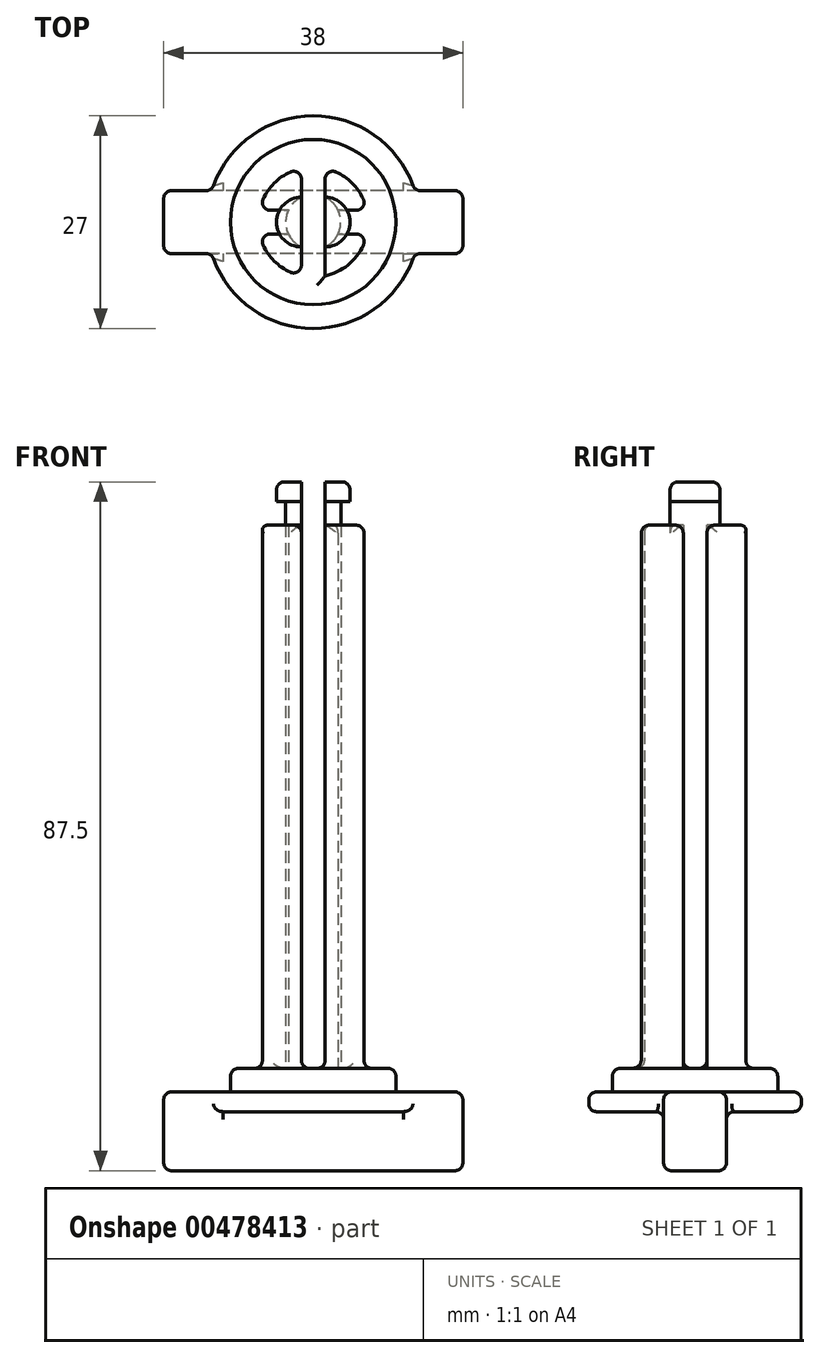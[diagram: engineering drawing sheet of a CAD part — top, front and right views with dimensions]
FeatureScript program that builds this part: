
annotation { "Feature Type Name" : "Feature", "Feature Type Description" : "" }
export const myFeature = defineFeature(function(context is Context, id is Id, definition is map)
    precondition{}
    {
        {
            var Q0;
            Q0=qCreatedBy(makeId("Top.planeOp"),FACE);
            var sketch = newSketch(context, id + "F0", { "sketchPlane" : qUnion([Q0])});
            skLineSegment(sketch, "E0.bottom", {"start": v(19, -4) * mm, "end": v(-19, -4) * mm});
            skLineSegment(sketch, "E0.top", {"start": v(19, 4) * mm, "end": v(-19, 4) * mm});
            skLineSegment(sketch, "E0.left", {"start": v(19, -4) * mm, "end": v(19, 4) * mm});
            skLineSegment(sketch, "E0.right", {"start": v(-19, -4) * mm, "end": v(-19, 4) * mm});
            skPoint(sketch, "E0.middle", {"position": v(0, 0) * mm});
            skSolve(sketch);
        }
        {
            var Q0;
            Q0 = qSketchRegion(id + "F0", true);
            extrude(context, id + "F1", {"entities" : qUnion([Q0]), "depth" : 10 * mm});
        }
        {
            var Q0;
            Q0=makeQuery(id+"F1.opExtrude","CAP_FACE",FACE,{"disambiguationData":[OSD([sQuery(id+"F0.wireOp",EDGE,"E0.bottom"),sQuery(id+"F0.wireOp",EDGE,"E0.top"),sQuery(id+"F0.wireOp",EDGE,"E0.left"),sQuery(id+"F0.wireOp",EDGE,"E0.right")])],"isStart":false});
            var sketch = newSketch(context, id + "F2", { "sketchPlane" : qUnion([Q0])});
            skCircle(sketch, "E1", {"center": v(0, 0) * mm, "radius": 13.5 * mm});
            skSolve(sketch);
        }
        {
            var Q0;
            Q0 = qSketchRegion(id + "F2", true);
            extrude(context, id + "F3", {"entities" : qUnion([Q0]), "operationType" : NewBodyOperationType.ADD, "depth" : -2.5 * mm});
        }
        {
            var Q0;
            Q0=makeQuery(id+"F3.boolean.opBoolean","MERGE",FACE,{"derivedFrom":[makeQuery(id+"F1.opExtrude","CAP_FACE",FACE,{"disambiguationData":[OSD([sQuery(id+"F0.wireOp",EDGE,"E0.bottom"),sQuery(id+"F0.wireOp",EDGE,"E0.top"),sQuery(id+"F0.wireOp",EDGE,"E0.left"),sQuery(id+"F0.wireOp",EDGE,"E0.right")])],"isStart":false}),makeQuery(id+"F3.opExtrude","CAP_FACE",FACE,{"disambiguationData":[OSD([sQuery(id+"F2.wireOp",EDGE,"E1")])],"isStart":true})]});
            var sketch = newSketch(context, id + "F4", { "sketchPlane" : qUnion([Q0])});
            skCircle(sketch, "E2", {"center": v(0, 0) * mm, "radius": 10.5 * mm});
            skSolve(sketch);
        }
        {
            var Q0;
            Q0 = qSketchRegion(id + "F4", true);
            extrude(context, id + "F5", {"entities" : qUnion([Q0]), "operationType" : NewBodyOperationType.ADD, "depth" : 3 * mm});
        }
        {
            var Q0;
            Q0=makeQuery(id+"F3.boolean.opBoolean","MERGE",FACE,{"derivedFrom":[makeQuery(id+"F1.opExtrude","CAP_FACE",FACE,{"disambiguationData":[OSD([sQuery(id+"F0.wireOp",EDGE,"E0.bottom"),sQuery(id+"F0.wireOp",EDGE,"E0.top"),sQuery(id+"F0.wireOp",EDGE,"E0.left"),sQuery(id+"F0.wireOp",EDGE,"E0.right")])],"isStart":false}),makeQuery(id+"F3.opExtrude","CAP_FACE",FACE,{"disambiguationData":[OSD([sQuery(id+"F2.wireOp",EDGE,"E1")])],"isStart":true})]});
            var sketch = newSketch(context, id + "F6", { "sketchPlane" : qUnion([Q0])});
            skArc(sketch, "E3", {"start": v(6.84, 1.5) * mm, "mid": v(0, 7) * mm, "end": v(-6.84, 1.5) * mm, "construction": true});
            skLineSegment(sketch, "E4.bottom", {"start": v(-1.5, -6.84) * mm, "end": v(1.5, -6.84) * mm, "construction": true});
            skLineSegment(sketch, "E4.top", {"start": v(-1.5, 6.84) * mm, "end": v(1.5, 6.84) * mm, "construction": true});
            skLineSegment(sketch, "E4.left", {"start": v(-1.5, -6.84) * mm, "end": v(-1.5, 6.84) * mm, "construction": true});
            skLineSegment(sketch, "E4.right", {"start": v(1.5, -6.84) * mm, "end": v(1.5, 6.84) * mm, "construction": true});
            skArc(sketch, "E5", {"start": v(1.5, -6.84) * mm, "mid": v(4.95, -4.95) * mm, "end": v(6.84, -1.5) * mm});
            skArc(sketch, "E6", {"start": v(-1.5, 6.84) * mm, "mid": v(-4.95, 4.95) * mm, "end": v(-6.84, 1.5) * mm});
            skLineSegment(sketch, "E7", {"start": v(1.5, 6.84) * mm, "end": v(1.5, -6.84) * mm});
            skLineSegment(sketch, "E8", {"start": v(-1.5, -6.84) * mm, "end": v(-1.5, 6.84) * mm});
            skCircle(sketch, "E9", {"center": v(0, 0) * mm, "radius": 3.5 * mm, "construction": true});
            skLineSegment(sketch, "E10.bottom", {"start": v(-6.84, 1.5) * mm, "end": v(6.84, 1.5) * mm, "construction": true});
            skLineSegment(sketch, "E10.top", {"start": v(-6.84, -1.5) * mm, "end": v(6.84, -1.5) * mm, "construction": true});
            skLineSegment(sketch, "E10.left", {"start": v(-6.84, 1.5) * mm, "end": v(-6.84, -1.5) * mm, "construction": true});
            skLineSegment(sketch, "E10.right", {"start": v(6.84, 1.5) * mm, "end": v(6.84, -1.5) * mm, "construction": true});
            skArc(sketch, "E11", {"start": v(-3.16, -1.5) * mm, "mid": v(-3.5, 0) * mm, "end": v(-3.16, 1.5) * mm});
            skArc(sketch, "E12", {"start": v(3.16, -1.5) * mm, "mid": v(3.5, 0) * mm, "end": v(3.16, 1.5) * mm});
            skLineSegment(sketch, "E13", {"start": v(-3.16, -1.5) * mm, "end": v(-6.84, -1.5) * mm});
            skLineSegment(sketch, "E14", {"start": v(-3.16, 1.5) * mm, "end": v(-6.84, 1.5) * mm});
            skLineSegment(sketch, "E15", {"start": v(3.16, 1.5) * mm, "end": v(6.84, 1.5) * mm});
            skLineSegment(sketch, "E16", {"start": v(3.16, -1.5) * mm, "end": v(6.84, -1.5) * mm});
            skArc(sketch, "E17.trimOffspring", {"start": v(-6.84, -1.5) * mm, "mid": v(0, -7) * mm, "end": v(6.84, -1.5) * mm, "construction": true});
            skArc(sketch, "E18.trimOffspring", {"start": v(-6.84, -1.5) * mm, "mid": v(-4.95, -4.95) * mm, "end": v(-1.5, -6.84) * mm});
            skArc(sketch, "E19.trimOffspring", {"start": v(6.84, 1.5) * mm, "mid": v(4.95, 4.95) * mm, "end": v(1.5, 6.84) * mm});
            skSolve(sketch);
        }
        {
            var Q0;
            Q0 = qSketchRegion(id + "F6", true);
            extrude(context, id + "F7", {"entities" : qUnion([Q0]), "operationType" : NewBodyOperationType.ADD, "depth" : 72 * mm});
        }
        {
            var Q0;
            Q0=makeQuery(id+"F7.opExtrude","CAP_FACE",FACE,{"disambiguationData":[OSD([sQuery(id+"F6.wireOp",EDGE,"E5"),sQuery(id+"F6.wireOp",EDGE,"E7")])],"isStart":false});
            var sketch = newSketch(context, id + "F8", { "sketchPlane" : qUnion([Q0])});
            skLineSegment(sketch, "E20.0", {"start": v(1.5, -6.84) * mm, "end": v(1.5, -6.84) * mm});
            skLineSegment(sketch, "E21.0", {"start": v(-1.5, 6.84) * mm, "end": v(-1.5, 6.84) * mm});
            skCircle(sketch, "E22", {"center": v(0, 0) * mm, "radius": 3.5 * mm, "construction": true});
            skArc(sketch, "E23", {"start": v(1.5, -3.16) * mm, "mid": v(3.5, 0) * mm, "end": v(1.5, 3.16) * mm});
            skArc(sketch, "E24", {"start": v(-1.5, 3.16) * mm, "mid": v(-3.5, 0) * mm, "end": v(-1.5, -3.16) * mm});
            skLineSegment(sketch, "E25", {"start": v(1.5, -3.16) * mm, "end": v(1.5, 3.16) * mm});
            skLineSegment(sketch, "E26", {"start": v(-1.5, 3.16) * mm, "end": v(-1.5, -3.16) * mm});
            skSolve(sketch);
        }
        {
            var Q0;
            Q0 = qSketchRegion(id + "F8", true);
            extrude(context, id + "F9", {"entities" : qUnion([Q0]), "operationType" : NewBodyOperationType.ADD, "depth" : 3 * mm});
        }
        {
            var Q0;
            Q0=makeQuery(id+"F9.opExtrude","CAP_FACE",FACE,{"disambiguationData":[OSD([sQuery(id+"F8.wireOp",EDGE,"E24"),sQuery(id+"F8.wireOp",EDGE,"E26")])],"isStart":false});
            var sketch = newSketch(context, id + "F10", { "sketchPlane" : qUnion([Q0])});
            skLineSegment(sketch, "E27.0", {"start": v(1.5, -3.16) * mm, "end": v(1.5, -6.84) * mm, "construction": true});
            skLineSegment(sketch, "E28.0", {"start": v(1.5, 3.16) * mm, "end": v(1.5, -3.16) * mm, "construction": true});
            skLineSegment(sketch, "E29.0", {"start": v(-1.5, 3.16) * mm, "end": v(-1.5, -3.16) * mm, "construction": true});
            skPoint(sketch, "E30.0", {"position": v(0, 0) * mm});
            skArc(sketch, "E31", {"start": v(1.5, 3.16) * mm, "mid": v(4.66, 0) * mm, "end": v(1.5, -3.16) * mm});
            skArc(sketch, "E32", {"start": v(-1.5, -3.16) * mm, "mid": v(-4.66, 0) * mm, "end": v(-1.5, 3.16) * mm});
            skLineSegment(sketch, "E33", {"start": v(-1.5, 3.16) * mm, "end": v(-1.5, -3.16) * mm});
            skLineSegment(sketch, "E34", {"start": v(1.5, -3.16) * mm, "end": v(1.5, 3.16) * mm});
            skSolve(sketch);
        }
        {
            var Q0;
            Q0 = qSketchRegion(id + "F10", true);
            extrude(context, id + "F11", {"entities" : qUnion([Q0]), "operationType" : NewBodyOperationType.ADD, "depth" : 2.5 * mm});
        }
        {
            var Q0;
            Q0=makeQuery(id+"F7.opExtrude","CAP_EDGE",EDGE,{"disambiguationData":[OSD([sQuery(id+"F6.wireOp",EDGE,"E5")])],"isStart":false});
            var Q1;
            Q1=makeQuery(id+"F7.opExtrude","CAP_EDGE",EDGE,{"disambiguationData":[OSD([sQuery(id+"F6.wireOp",EDGE,"E6")])],"isStart":false});
            var Q2;
            Q2=makeQuery(id+"F11.opExtrude","CAP_EDGE",EDGE,{"disambiguationData":[OSD([sQuery(id+"F10.wireOp",EDGE,"OLtfRIEC-O7za-MDvR-deQH-UAJOeCopyKRy")])],"isStart":false});
            var Q3;
            Q3=makeQuery(id+"F11.opExtrude","CAP_EDGE",EDGE,{"disambiguationData":[OSD([sQuery(id+"F10.wireOp",EDGE,"Nmxz0keU-6gQF-4ana-PDwX-EkidwWlCpvxk")])],"isStart":false});
            var Q4;
            Q4=makeQuery(id+"F7.boolean.opBoolean","INTERSECT",EDGE,{"derivedFrom":[makeQuery(id+"F5.opExtrude","CAP_FACE",FACE,{"disambiguationData":[OSD([sQuery(id+"F4.wireOp",EDGE,"E2")])],"isStart":false}),makeQuery(id+"F7.opExtrude","SWEPT_FACE",FACE,{"disambiguationData":[OSD([sQuery(id+"F6.wireOp",EDGE,"E6")])]})]});
            var Q5;
            Q5=makeQuery(id+"F7.boolean.opBoolean","INTERSECT",EDGE,{"derivedFrom":[makeQuery(id+"F5.opExtrude","CAP_FACE",FACE,{"disambiguationData":[OSD([sQuery(id+"F4.wireOp",EDGE,"E2")])],"isStart":false}),makeQuery(id+"F7.opExtrude","SWEPT_FACE",FACE,{"disambiguationData":[OSD([sQuery(id+"F6.wireOp",EDGE,"E5")])]})]});
            var Q6;
            Q6=makeQuery(id+"F7.boolean.opBoolean","INTERSECT",EDGE,{"derivedFrom":[makeQuery(id+"F5.opExtrude","CAP_FACE",FACE,{"disambiguationData":[OSD([sQuery(id+"F4.wireOp",EDGE,"E2")])],"isStart":false}),makeQuery(id+"F7.opExtrude","SWEPT_FACE",FACE,{"disambiguationData":[OSD([sQuery(id+"F6.wireOp",EDGE,"E8")])]})]});
            var Q7;
            Q7=makeQuery(id+"F7.boolean.opBoolean","INTERSECT",EDGE,{"derivedFrom":[makeQuery(id+"F5.opExtrude","CAP_FACE",FACE,{"disambiguationData":[OSD([sQuery(id+"F4.wireOp",EDGE,"E2")])],"isStart":false}),makeQuery(id+"F7.opExtrude","SWEPT_FACE",FACE,{"disambiguationData":[OSD([sQuery(id+"F6.wireOp",EDGE,"E7")])]})]});
            var Q8;
            Q8=makeQuery(id+"F5.opExtrude","CAP_EDGE",EDGE,{"disambiguationData":[OSD([sQuery(id+"F4.wireOp",EDGE,"E2")])],"isStart":false});
            var Q9;
            {var subQ0=sQuery(id+"F0.wireOp",EDGE,"E0.top");var subQ1=sQuery(id+"F2.wireOp",EDGE,"E1");Q9=makeQuery(id+"F3.boolean.opBoolean","SPLIT",EDGE,{"disambiguationData":[TD([makeQuery(id+"F1.opExtrude","SWEPT_FACE",FACE,{"disambiguationData":[OSD([subQ0])]})])],"derivedFrom":makeQuery(id+"F3.opExtrude","CAP_EDGE",EDGE,{"disambiguationData":[OSD([subQ1])],"isStart":true})});}
            var Q10;
            {var subQ0=sQuery(id+"F0.wireOp",EDGE,"E0.right");var subQ2=sQuery(id+"F0.wireOp",EDGE,"E0.top");Q10=makeQuery(id+"F3.boolean.opBoolean","SPLIT",EDGE,{"disambiguationData":[TD([makeQuery(id+"F1.opExtrude","SWEPT_FACE",FACE,{"disambiguationData":[OSD([subQ0])]})])],"derivedFrom":makeQuery(id+"F1.opExtrude","CAP_EDGE",EDGE,{"disambiguationData":[OSD([subQ2])],"isStart":false})});}
            var Q11;
            Q11=makeQuery(id+"F1.opExtrude","CAP_EDGE",EDGE,{"disambiguationData":[OSD([sQuery(id+"F0.wireOp",EDGE,"E0.right")])],"isStart":false});
            var Q12;
            Q12=makeQuery(id+"F1.opExtrude","SWEPT_EDGE",EDGE,{"disambiguationData":[OSD([sQuery(id+"F0.wireOp",EDGE,"E0.top"),sQuery(id+"F0.wireOp",EDGE,"E0.right")])]});
            var Q13;
            Q13=makeQuery(id+"F3.boolean.opBoolean","INTERSECT",EDGE,{"disambiguationData":[OD(1.0)],"derivedFrom":[makeQuery(id+"F1.opExtrude","SWEPT_FACE",FACE,{"disambiguationData":[OSD([sQuery(id+"F0.wireOp",EDGE,"E0.top")])]}),makeQuery(id+"F3.opExtrude","SWEPT_FACE",FACE,{"disambiguationData":[OSD([sQuery(id+"F2.wireOp",EDGE,"E1")])]})]});
            var Q14;
            {var subQ0=sQuery(id+"F0.wireOp",EDGE,"E0.left");var subQ2=sQuery(id+"F0.wireOp",EDGE,"E0.top");Q14=makeQuery(id+"F3.boolean.opBoolean","SPLIT",EDGE,{"disambiguationData":[TD([makeQuery(id+"F1.opExtrude","SWEPT_FACE",FACE,{"disambiguationData":[OSD([subQ0])]})])],"derivedFrom":makeQuery(id+"F1.opExtrude","CAP_EDGE",EDGE,{"disambiguationData":[OSD([subQ2])],"isStart":false})});}
            var Q15;
            Q15=makeQuery(id+"F3.boolean.opBoolean","INTERSECT",EDGE,{"disambiguationData":[OD(0.0)],"derivedFrom":[makeQuery(id+"F1.opExtrude","SWEPT_FACE",FACE,{"disambiguationData":[OSD([sQuery(id+"F0.wireOp",EDGE,"E0.top")])]}),makeQuery(id+"F3.opExtrude","SWEPT_FACE",FACE,{"disambiguationData":[OSD([sQuery(id+"F2.wireOp",EDGE,"E1")])]})]});
            var Q16;
            Q16=makeQuery(id+"F1.opExtrude","CAP_EDGE",EDGE,{"disambiguationData":[OSD([sQuery(id+"F0.wireOp",EDGE,"E0.left")])],"isStart":false});
            var Q17;
            {var subQ1=sQuery(id+"F0.wireOp",EDGE,"E0.left");var subQ2=sQuery(id+"F0.wireOp",EDGE,"E0.bottom");Q17=makeQuery(id+"F3.boolean.opBoolean","SPLIT",EDGE,{"disambiguationData":[TD([makeQuery(id+"F1.opExtrude","SWEPT_FACE",FACE,{"disambiguationData":[OSD([subQ1])]})])],"derivedFrom":makeQuery(id+"F1.opExtrude","CAP_EDGE",EDGE,{"disambiguationData":[OSD([subQ2])],"isStart":false})});}
            var Q18;
            {var subQ0=sQuery(id+"F0.wireOp",EDGE,"E0.bottom");var subQ1=sQuery(id+"F2.wireOp",EDGE,"E1");Q18=makeQuery(id+"F3.boolean.opBoolean","SPLIT",EDGE,{"disambiguationData":[TD([makeQuery(id+"F1.opExtrude","SWEPT_FACE",FACE,{"disambiguationData":[OSD([subQ0])]})])],"derivedFrom":makeQuery(id+"F3.opExtrude","CAP_EDGE",EDGE,{"disambiguationData":[OSD([subQ1])],"isStart":true})});}
            var Q19;
            Q19=makeQuery(id+"F3.boolean.opBoolean","INTERSECT",EDGE,{"disambiguationData":[OD(0.0)],"derivedFrom":[makeQuery(id+"F1.opExtrude","SWEPT_FACE",FACE,{"disambiguationData":[OSD([sQuery(id+"F0.wireOp",EDGE,"E0.bottom")])]}),makeQuery(id+"F3.opExtrude","SWEPT_FACE",FACE,{"disambiguationData":[OSD([sQuery(id+"F2.wireOp",EDGE,"E1")])]})]});
            var Q20;
            Q20=makeQuery(id+"F3.boolean.opBoolean","INTERSECT",EDGE,{"disambiguationData":[OD(1.0)],"derivedFrom":[makeQuery(id+"F1.opExtrude","SWEPT_FACE",FACE,{"disambiguationData":[OSD([sQuery(id+"F0.wireOp",EDGE,"E0.bottom")])]}),makeQuery(id+"F3.opExtrude","SWEPT_FACE",FACE,{"disambiguationData":[OSD([sQuery(id+"F2.wireOp",EDGE,"E1")])]})]});
            var Q21;
            {var subQ0=sQuery(id+"F2.wireOp",EDGE,"E1");Q21=makeQuery(id+"F3.boolean.opBoolean","SPLIT",EDGE,{"disambiguationData":[TD([makeQuery(id+"F1.opExtrude","SWEPT_FACE",FACE,{"disambiguationData":[OSD([sQuery(id+"F0.wireOp",EDGE,"E0.bottom")])]})])],"derivedFrom":makeQuery(id+"F3.opExtrude","CAP_EDGE",EDGE,{"disambiguationData":[OSD([subQ0])],"isStart":false})});}
            var Q22;
            Q22=makeQuery(id+"F1.opExtrude","SWEPT_FACE",FACE,{"disambiguationData":[OSD([sQuery(id+"F0.wireOp",EDGE,"E0.bottom")])]});
            var Q23;
            Q23=makeQuery(id+"F1.opExtrude","SWEPT_FACE",FACE,{"disambiguationData":[OSD([sQuery(id+"F0.wireOp",EDGE,"E0.top")])]});
            var Q24;
            {var subQ0=sQuery(id+"F2.wireOp",EDGE,"E1");Q24=makeQuery(id+"F3.boolean.opBoolean","SPLIT",FACE,{"disambiguationData":[TD([makeQuery(id+"F1.opExtrude","SWEPT_FACE",FACE,{"disambiguationData":[OSD([sQuery(id+"F0.wireOp",EDGE,"E0.top")])]})])],"derivedFrom":makeQuery(id+"F3.opExtrude","CAP_FACE",FACE,{"disambiguationData":[OSD([subQ0])],"isStart":false})});}
            var Q25;
            Q25=makeQuery(id+"F1.opExtrude","SWEPT_FACE",FACE,{"disambiguationData":[OSD([sQuery(id+"F0.wireOp",EDGE,"E0.left")])]});
            var Q26;
            Q26=makeQuery(id+"F1.opExtrude","SWEPT_FACE",FACE,{"disambiguationData":[OSD([sQuery(id+"F0.wireOp",EDGE,"E0.right")])]});
            var Q27;
            Q27=makeQuery(id+"F7.boolean.opBoolean","INTERSECT",EDGE,{"derivedFrom":[makeQuery(id+"F5.opExtrude","CAP_FACE",FACE,{"disambiguationData":[OSD([sQuery(id+"F4.wireOp",EDGE,"E2")])],"isStart":false}),makeQuery(id+"F7.opExtrude","SWEPT_FACE",FACE,{"disambiguationData":[OSD([sQuery(id+"F6.wireOp",EDGE,"E18.trimOffspring")])]})]});
            var Q28;
            Q28=makeQuery(id+"F7.opExtrude","SWEPT_FACE",FACE,{"disambiguationData":[OSD([sQuery(id+"F6.wireOp",EDGE,"E19.trimOffspring")])]});
            var Q29;
            Q29=makeQuery(id+"F7.opExtrude","SWEPT_FACE",FACE,{"disambiguationData":[OSD([sQuery(id+"F6.wireOp",EDGE,"E6")])]});
            var Q30;
            Q30=makeQuery(id+"F7.opExtrude","SWEPT_FACE",FACE,{"disambiguationData":[OSD([sQuery(id+"F6.wireOp",EDGE,"E18.trimOffspring")])]});
            var Q31;
            Q31=makeQuery(id+"F7.opExtrude","CAP_EDGE",EDGE,{"disambiguationData":[OSD([sQuery(id+"F6.wireOp",EDGE,"E16")])],"isStart":false});
            var Q32;
            Q32=makeQuery(id+"F7.opExtrude","SWEPT_EDGE",EDGE,{"disambiguationData":[OSD([sQuery(id+"F6.wireOp",EDGE,"E5"),sQuery(id+"F6.wireOp",EDGE,"E16")])]});
            var Q33;
            Q33=makeQuery(id+"F7.opExtrude","CAP_EDGE",EDGE,{"disambiguationData":[OSD([sQuery(id+"F6.wireOp",EDGE,"E15")])],"isStart":false});
            var Q34;
            {var subQ0=sQuery(id+"F6.wireOp",EDGE,"E18.trimOffspring");var subQ2=sQuery(id+"F6.wireOp",EDGE,"E8");Q34=makeQuery(id+"F9.boolean.opBoolean","SPLIT",EDGE,{"disambiguationData":[TD([makeQuery(id+"F7.opExtrude","SWEPT_FACE",FACE,{"disambiguationData":[OSD([subQ0])]})])],"derivedFrom":makeQuery(id+"F7.opExtrude","CAP_EDGE",EDGE,{"disambiguationData":[OSD([subQ2])],"isStart":false})});}
            var Q35;
            Q35=makeQuery(id+"F11.opExtrude","CAP_EDGE",EDGE,{"disambiguationData":[OSD([sQuery(id+"F10.wireOp",EDGE,"E32")])],"isStart":false});
            var Q36;
            Q36=makeQuery(id+"F11.opExtrude","CAP_EDGE",EDGE,{"disambiguationData":[OSD([sQuery(id+"F10.wireOp",EDGE,"E31")])],"isStart":false});
            fillet(context, id + "F12", {"entities" : qUnion([Q0, Q1, Q2, Q3, Q4, Q5, Q6, Q7, Q8, Q9, Q10, Q11, Q12, Q13, Q14, Q15, Q16, Q17, Q18, Q19, Q20, Q21, Q22, Q23, Q24, Q25, Q26, Q27, Q28, Q29, Q30, Q31, Q32, Q33, Q34, Q35, Q36]), "radius" : 1 * mm, "tangentPropagation" : true, "allowEdgeOverflow" : false});
        }
    });
